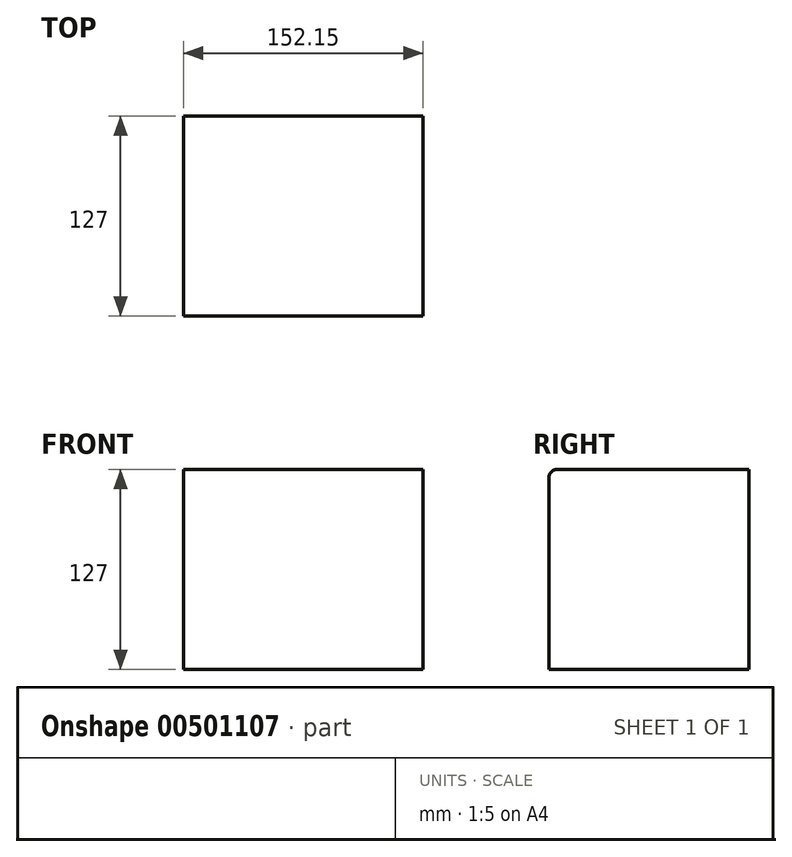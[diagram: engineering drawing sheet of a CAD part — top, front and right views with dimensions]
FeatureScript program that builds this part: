
annotation { "Feature Type Name" : "Feature", "Feature Type Description" : "" }
export const myFeature = defineFeature(function(context is Context, id is Id, definition is map)
    precondition{}
    {
        {
            var Q0;
            Q0=qCreatedBy(makeId("Front.planeOp"),FACE);
            var sketch = newSketch(context, id + "F0", { "sketchPlane" : qUnion([Q0])});
            skLineSegment(sketch, "E0.bottom", {"start": v(-58.3, 85.5) * mm, "end": v(68.7, 85.5) * mm});
            skLineSegment(sketch, "E0.top", {"start": v(-58.3, -41.5) * mm, "end": v(68.7, -41.5) * mm});
            skLineSegment(sketch, "E0.left", {"start": v(-58.3, 85.5) * mm, "end": v(-58.3, -41.5) * mm});
            skLineSegment(sketch, "E0.right", {"start": v(68.7, 85.5) * mm, "end": v(68.7, -41.5) * mm});
            skSolve(sketch);
        }
        {
            var Q0;
            Q0=makeQuery(id+"F0.imprint","IMPRINT",FACE,{"disambiguationData":[TD([[makeQuery(id+"F0.imprint","IMPRINT",EDGE,{"derivedFrom":sQuery(id+"F0.wireOp",EDGE,"E0.bottom")}),-1.0]])]});
            extrude(context, id + "F1", {"entities" : qUnion([Q0]), "depth" : 127 * mm});
        }
        {
            var Q0;
            Q0=makeQuery(id+"F1.opExtrude","SWEPT_FACE",FACE,{"disambiguationData":[OSD([sQuery(id+"F0.wireOp",EDGE,"E0.right")])]});
            extrude(context, id + "F2", {"entities" : qUnion([Q0]), "operationType" : NewBodyOperationType.ADD, "depth" : 25.15 * mm});
        }
        {
            var Q0;
            {var subQ0=sQuery(id+"F0.wireOp",EDGE,"E0.right");var subQ1=sQuery(id+"F0.wireOp",EDGE,"E0.bottom");Q0=makeQuery(id+"F2.boolean.opBoolean","MERGE",EDGE,{"derivedFrom":[makeQuery(id+"F1.opExtrude","CAP_EDGE",EDGE,{"disambiguationData":[OSD([subQ1])],"isStart":false}),makeQuery(id+"F2.opExtrude","SWEPT_EDGE",EDGE,{"disambiguationData":[OSD([subQ1,subQ0]),TDD([makeQuery(id+"F1.opExtrude","CAP_VERTEX",VERTEX,{"disambiguationData":[OSD([subQ1,subQ0])],"isStart":false})])]})]});}
            fillet(context, id + "F3", {"entities" : qUnion([Q0]), "radius" : 5.08 * mm, "tangentPropagation" : true, "allowEdgeOverflow" : false});
        }
    });
